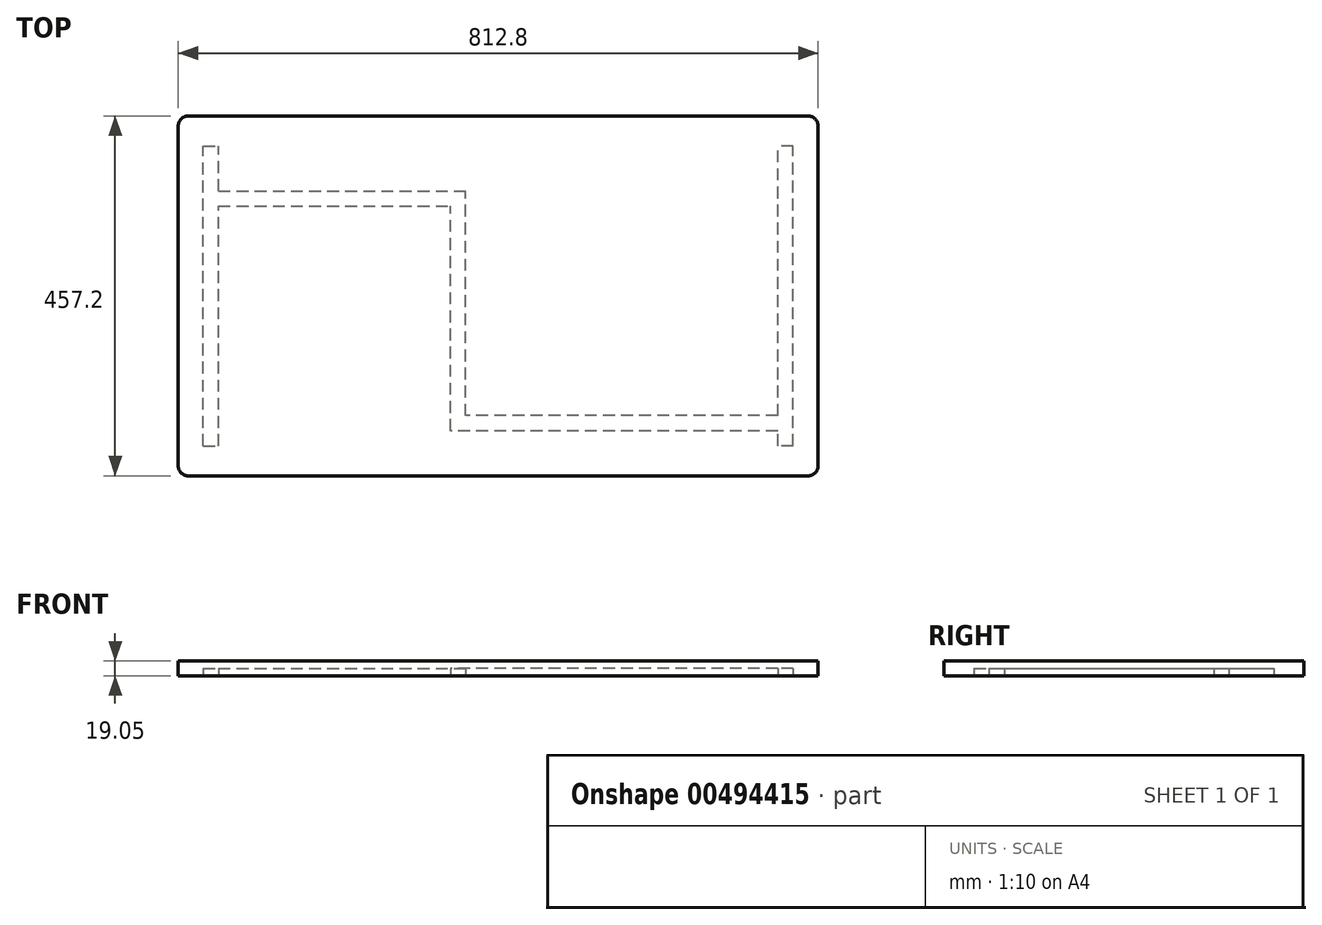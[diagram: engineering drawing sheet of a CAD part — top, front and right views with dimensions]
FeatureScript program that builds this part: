
annotation { "Feature Type Name" : "Feature", "Feature Type Description" : "" }
export const myFeature = defineFeature(function(context is Context, id is Id, definition is map)
    precondition{}
    {
        {
            var Q0;
            Q0=qCreatedBy(makeId("Top.planeOp"),FACE);
            var sketch = newSketch(context, id + "F0", { "sketchPlane" : qUnion([Q0])});
            skLineSegment(sketch, "E0.bottom", {"start": v(-406.4, 228.6) * mm, "end": v(406.4, 228.6) * mm});
            skLineSegment(sketch, "E0.top", {"start": v(-406.4, -228.6) * mm, "end": v(406.4, -228.6) * mm});
            skLineSegment(sketch, "E0.left", {"start": v(-406.4, 228.6) * mm, "end": v(-406.4, -228.6) * mm});
            skLineSegment(sketch, "E0.right", {"start": v(406.4, 228.6) * mm, "end": v(406.4, -228.6) * mm});
            skPoint(sketch, "E0.middle", {"position": v(0, 0) * mm});
            skSolve(sketch);
        }
        {
            var Q0;
            Q0 = qSketchRegion(id + "F0", true);
            extrude(context, id + "F1", {"entities" : qUnion([Q0]), "depth" : 19.05 * mm, "offsetDistance" : 25.4 * mm});
        }
        {
            var Q0;
            Q0=makeQuery(id+"F1.opExtrude","SWEPT_EDGE",EDGE,{"disambiguationData":[OSD([sQuery(id+"F0.wireOp",EDGE,"E0.top"),sQuery(id+"F0.wireOp",EDGE,"E0.left")])]});
            var Q1;
            Q1=makeQuery(id+"F1.opExtrude","SWEPT_EDGE",EDGE,{"disambiguationData":[OSD([sQuery(id+"F0.wireOp",EDGE,"E0.top"),sQuery(id+"F0.wireOp",EDGE,"E0.right")])]});
            var Q2;
            Q2=makeQuery(id+"F1.opExtrude","SWEPT_EDGE",EDGE,{"disambiguationData":[OSD([sQuery(id+"F0.wireOp",EDGE,"E0.bottom"),sQuery(id+"F0.wireOp",EDGE,"E0.right")])]});
            var Q3;
            Q3=makeQuery(id+"F1.opExtrude","SWEPT_EDGE",EDGE,{"disambiguationData":[OSD([sQuery(id+"F0.wireOp",EDGE,"E0.bottom"),sQuery(id+"F0.wireOp",EDGE,"E0.left")])]});
            fillet(context, id + "F2", {"entities" : qUnion([Q0, Q1, Q2, Q3]), "radius" : 12.7 * mm, "tangentPropagation" : true, "allowEdgeOverflow" : false});
        }
        {
            var Q0;
            Q0=makeQuery(id+"F1.opExtrude","CAP_FACE",FACE,{"disambiguationData":[OSD([sQuery(id+"F0.wireOp",EDGE,"E0.bottom"),sQuery(id+"F0.wireOp",EDGE,"E0.top"),sQuery(id+"F0.wireOp",EDGE,"E0.left"),sQuery(id+"F0.wireOp",EDGE,"E0.right")])],"isStart":true});
            var sketch = newSketch(context, id + "F3", { "sketchPlane" : qUnion([Q0])});
            skLineSegment(sketch, "E1", {"start": v(-406.4, -52.2) * mm, "end": v(-365.13, -52.2) * mm, "construction": true});
            skLineSegment(sketch, "E2.MirrorCS", {"start": v(406.4, -52.2) * mm, "end": v(365.13, -52.2) * mm, "construction": true});
            skLineSegment(sketch, "E3", {"start": v(14.27, -228.6) * mm, "end": v(14.27, -133.35) * mm, "construction": true});
            skLineSegment(sketch, "E4.MirrorCS", {"start": v(14.27, 228.6) * mm, "end": v(14.27, 133.35) * mm, "construction": true});
            skLineSegment(sketch, "E5.bottom", {"start": v(-365.13, 133.35) * mm, "end": v(365.13, 133.35) * mm, "construction": true});
            skLineSegment(sketch, "E5.top", {"start": v(-365.13, -133.35) * mm, "end": v(365.13, -133.35) * mm, "construction": true});
            skLineSegment(sketch, "E5.left", {"start": v(-365.13, 133.35) * mm, "end": v(-365.13, -133.35) * mm, "construction": true});
            skLineSegment(sketch, "E5.right", {"start": v(365.13, 133.35) * mm, "end": v(365.13, -133.35) * mm, "construction": true});
            skLineSegment(sketch, "E6.bottom", {"start": v(-60.72, 133.35) * mm, "end": v(-41.28, 133.35) * mm});
            skLineSegment(sketch, "E6.top", {"start": v(-60.72, -133.35) * mm, "end": v(-41.28, -133.35) * mm});
            skLineSegment(sketch, "E6.left", {"start": v(-60.72, 133.35) * mm, "end": v(-60.72, -133.35) * mm});
            skLineSegment(sketch, "E6.right", {"start": v(-41.28, 133.35) * mm, "end": v(-41.28, -133.35) * mm});
            skLineSegment(sketch, "E7.top", {"start": v(-60.72, 152) * mm, "end": v(-41.28, 152) * mm});
            skLineSegment(sketch, "E7.left", {"start": v(-60.72, 133.35) * mm, "end": v(-60.72, 152) * mm});
            skLineSegment(sketch, "E7.right", {"start": v(-41.28, 133.35) * mm, "end": v(-41.28, 152) * mm});
            skSolve(sketch);
        }
        {
            var Q0;
            Q0 = qSketchRegion(id + "F3", true);
            extrude(context, id + "F4", {"entities" : qUnion([Q0]), "operationType" : NewBodyOperationType.REMOVE, "oppositeDirection" : true, "depth" : 9.52 * mm, "offsetDistance" : 25.4 * mm});
        }
        {
            var Q0;
            Q0=makeQuery(id+"F1.opExtrude","CAP_FACE",FACE,{"disambiguationData":[OSD([sQuery(id+"F0.wireOp",EDGE,"E0.bottom"),sQuery(id+"F0.wireOp",EDGE,"E0.top"),sQuery(id+"F0.wireOp",EDGE,"E0.left"),sQuery(id+"F0.wireOp",EDGE,"E0.right")])],"isStart":true});
            var sketch = newSketch(context, id + "F5", { "sketchPlane" : qUnion([Q0])});
            skLineSegment(sketch, "E8", {"start": v(406.4, 27.26) * mm, "end": v(374.65, 27.26) * mm, "construction": true});
            skLineSegment(sketch, "E9", {"start": v(322.16, 228.6) * mm, "end": v(322.16, 190.5) * mm, "construction": true});
            skLineSegment(sketch, "E10.MirrorCS", {"start": v(322.16, -228.6) * mm, "end": v(322.16, -190.5) * mm, "construction": true});
            skLineSegment(sketch, "E11.bottom", {"start": v(374.65, 190.5) * mm, "end": v(355.2, 190.5) * mm});
            skLineSegment(sketch, "E11.top", {"start": v(374.65, -190.5) * mm, "end": v(355.2, -190.5) * mm});
            skLineSegment(sketch, "E11.left", {"start": v(374.65, 190.5) * mm, "end": v(374.65, -190.5) * mm});
            skLineSegment(sketch, "E11.right", {"start": v(355.2, 190.5) * mm, "end": v(355.2, -190.5) * mm});
            skLineSegment(sketch, "E12.MirrorCS", {"start": v(-355.2, 190.5) * mm, "end": v(-355.2, -190.5) * mm});
            skLineSegment(sketch, "E13.MirrorCS", {"start": v(-374.65, 190.5) * mm, "end": v(-374.65, -190.5) * mm});
            skLineSegment(sketch, "E14.MirrorCS", {"start": v(-374.65, 190.5) * mm, "end": v(-355.2, 190.5) * mm});
            skLineSegment(sketch, "E15.MirrorCS", {"start": v(-374.65, -190.5) * mm, "end": v(-355.2, -190.5) * mm});
            skSolve(sketch);
        }
        {
            var Q0;
            Q0 = qSketchRegion(id + "F5", true);
            extrude(context, id + "F6", {"entities" : qUnion([Q0]), "operationType" : NewBodyOperationType.REMOVE, "oppositeDirection" : true, "depth" : 9.52 * mm, "offsetDistance" : 25.4 * mm});
        }
        {
            var Q0;
            Q0=makeQuery(id+"F1.opExtrude","CAP_FACE",FACE,{"disambiguationData":[OSD([sQuery(id+"F0.wireOp",EDGE,"E0.bottom"),sQuery(id+"F0.wireOp",EDGE,"E0.top"),sQuery(id+"F0.wireOp",EDGE,"E0.left"),sQuery(id+"F0.wireOp",EDGE,"E0.right")])],"isStart":true});
            var sketch = newSketch(context, id + "F7", { "sketchPlane" : qUnion([Q0])});
            skLineSegment(sketch, "E16.bottom", {"start": v(-355.2, -133.35) * mm, "end": v(-41.28, -133.35) * mm});
            skLineSegment(sketch, "E16.top", {"start": v(-355.2, -113.9) * mm, "end": v(-41.28, -113.9) * mm});
            skLineSegment(sketch, "E16.left", {"start": v(-355.2, -133.35) * mm, "end": v(-355.2, -113.9) * mm});
            skLineSegment(sketch, "E16.right", {"start": v(-41.28, -133.35) * mm, "end": v(-41.28, -113.9) * mm});
            skLineSegment(sketch, "E17.bottom", {"start": v(355.2, 171.45) * mm, "end": v(-60.72, 171.45) * mm});
            skLineSegment(sketch, "E17.top", {"start": v(355.2, 152) * mm, "end": v(-60.72, 152) * mm});
            skLineSegment(sketch, "E17.left", {"start": v(355.2, 171.45) * mm, "end": v(355.2, 152) * mm});
            skLineSegment(sketch, "E17.right", {"start": v(-60.72, 171.45) * mm, "end": v(-60.72, 152) * mm});
            skSolve(sketch);
        }
        {
            var Q0;
            Q0 = qSketchRegion(id + "F7", true);
            extrude(context, id + "F8", {"entities" : qUnion([Q0]), "operationType" : NewBodyOperationType.REMOVE, "oppositeDirection" : true, "depth" : 9.52 * mm, "offsetDistance" : 25.4 * mm});
        }
    });
